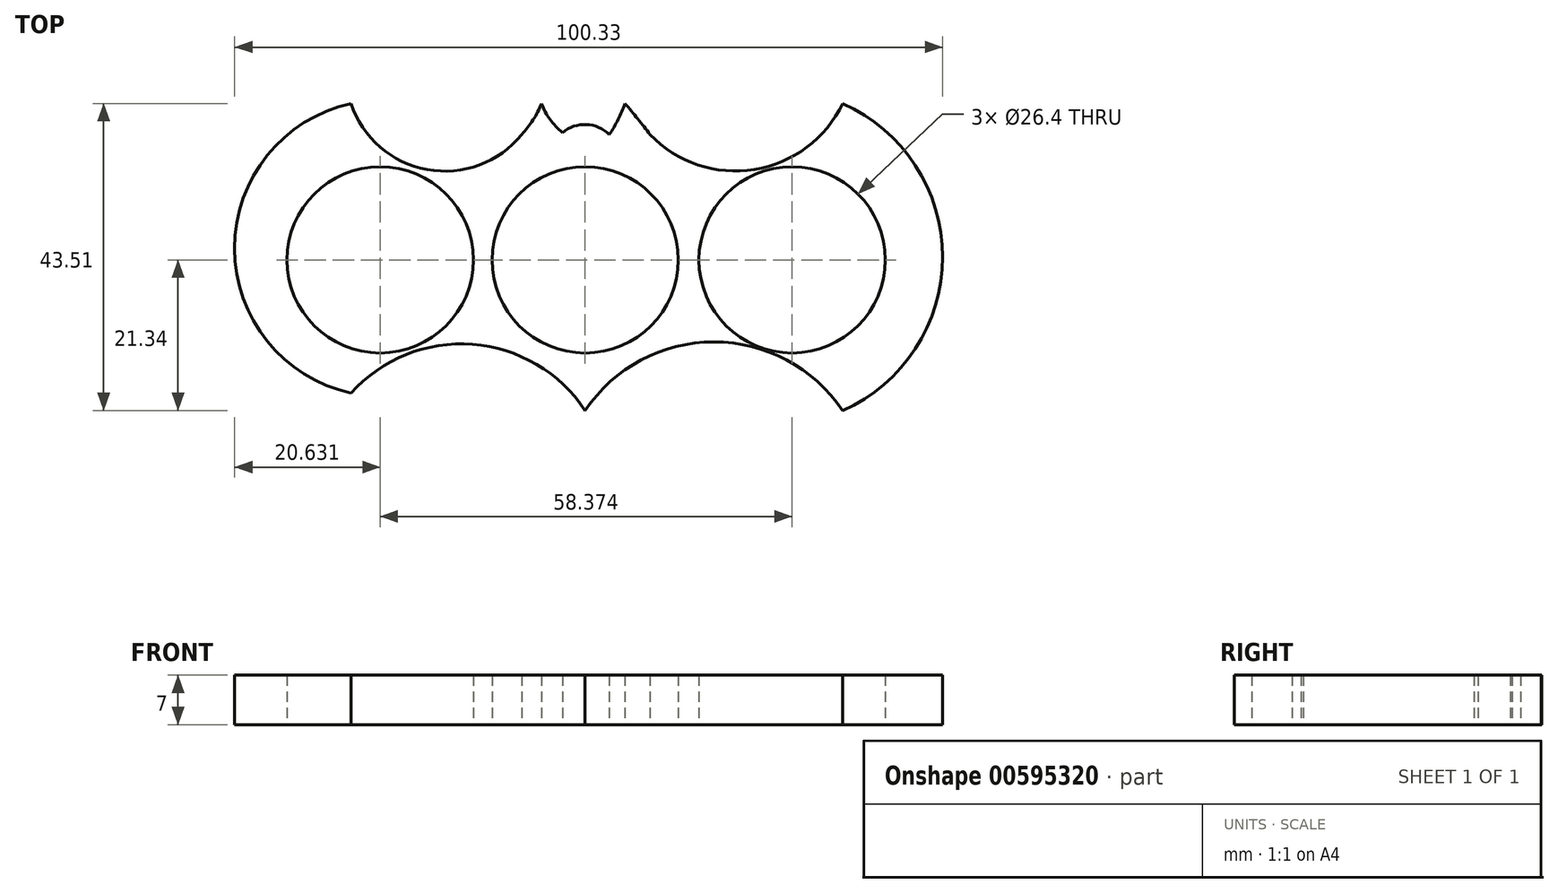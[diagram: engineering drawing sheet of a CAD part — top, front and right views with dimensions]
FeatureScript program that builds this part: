
annotation { "Feature Type Name" : "Feature", "Feature Type Description" : "" }
export const myFeature = defineFeature(function(context is Context, id is Id, definition is map)
    precondition{}
    {
        {
            var Q0;
            Q0=qCreatedBy(makeId("Top.planeOp"),FACE);
            var sketch = newSketch(context, id + "F0", { "sketchPlane" : qUnion([Q0])});
            skPoint(sketch, "E0.startSnap0", {"position": v(-8.68, 30.9) * mm});
            skCircle(sketch, "E1", {"center": v(0, 0) * mm, "radius": 11.2 * mm});
            skCircle(sketch, "E2", {"center": v(0, 0) * mm, "radius": 13.2 * mm});
            skCircle(sketch, "E3", {"center": v(29.32, 0) * mm, "radius": 11.2 * mm});
            skCircle(sketch, "E4", {"center": v(29.32, 0) * mm, "radius": 13.2 * mm});
            skCircle(sketch, "E5", {"center": v(-29.05, 0) * mm, "radius": 11.2 * mm});
            skCircle(sketch, "E6", {"center": v(-29.05, 0) * mm, "radius": 13.2 * mm});
            skArc(sketch, "E7", {"start": v(3.4, 17.75) * mm, "mid": v(0.16, 19.18) * mm, "end": v(-3.2, 18.02) * mm});
            skArc(sketch, "E8", {"start": v(-33.18, 22.16) * mm, "mid": v(-22.39, 12.8) * mm, "end": v(-9, 17.75) * mm});
            skArc(sketch, "E9", {"start": v(9.2, 17.75) * mm, "mid": v(24, 12.81) * mm, "end": v(36.48, 22.16) * mm});
            skArc(sketch, "E10", {"start": v(-33.18, 22.16) * mm, "mid": v(-49.68, 1.65) * mm, "end": v(-33.18, -18.86) * mm});
            skArc(sketch, "E11", {"start": v(36.48, -21.34) * mm, "mid": v(50.65, 0.4) * mm, "end": v(36.48, 22.16) * mm});
            skArc(sketch, "E12", {"start": v(0, -21.34) * mm, "mid": v(-15.98, -11.97) * mm, "end": v(-33.18, -18.86) * mm});
            skArc(sketch, "E13", {"start": v(36.48, -21.34) * mm, "mid": v(18.24, -11.62) * mm, "end": v(0, -21.34) * mm});
            skArc(sketch, "E14", {"start": v(-6.2, 22.17) * mm, "mid": v(-4.97, 19.9) * mm, "end": v(-3.2, 18.02) * mm});
            skArc(sketch, "E15", {"start": v(-9, 17.75) * mm, "mid": v(-7.38, 19.82) * mm, "end": v(-6.2, 22.17) * mm});
            skArc(sketch, "E16", {"start": v(3.4, 17.75) * mm, "mid": v(4.67, 19.89) * mm, "end": v(5.64, 22.17) * mm});
            skArc(sketch, "E17", {"start": v(9.2, 17.75) * mm, "mid": v(7.45, 19.98) * mm, "end": v(5.64, 22.17) * mm});
            skSolve(sketch);
        }
        {
            var Q0;
            Q0 = qSketchRegion(id + "F0", true);
            extrude(context, id + "F1", {"entities" : qUnion([Q0]), "depth" : 7 * mm, "offsetDistance" : 25 * mm});
        }
    });
